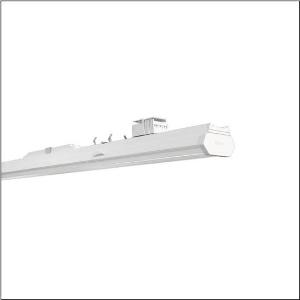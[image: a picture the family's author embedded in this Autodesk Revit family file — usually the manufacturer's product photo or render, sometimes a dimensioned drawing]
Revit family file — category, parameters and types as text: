
# Revit family: licross_r__11_protected_mo_51td117n485g_c933
name_source: partatom
category: Lighting Fixtures
units: mm (PartAtom-declared; Revit-internal decimal feet)

## family parameters
Cut with Voids When Loaded = No
Host = Face
Light Source = No
Part Type = Normal
Room Calculation Point = No
Round Connector Dimension = Use Diameter
Shared = No

## types (1)
- Licross® 11 Protected MO (1 x LED, 8680 lm, 48.6 W, 4000K)
    Apparent Load = 49 VA
    CIE Flux Codes = 83 94 98 100 100
    Color Rendering = 80
    Color Temperature = 4000K
    Default Elevation = 1800 mm
    Description = Licross® 11 Protected MO, luminaire insert, of sheet steel, galvanised, coil coated, white, length: 1.500mm, width: 90mm, height: 101mm, LED rated luminous flux: 8.680lm, light colour: 840, control gear: ON/OFF, with plug, 3-pole, with phase selection, mains connection: 220..240V, AC, 50/60Hz, rated input power: 49W, halogen-free wiring, primary light control with lens, of plastic, primary optical cover: cover, of PMMA, light emission: direct distribution, primary light characteristic: symmetric, protection rating (complete): IP54, insulation class (complete): insulation class I (protective earthing), certification: CE, ENEC, VDE, UKCA, protection symbol: D if used in an environment with non-conductive dust loads with corresponding accessories, impact resistance: IK06, permissible ambient temperature for indoor applications: -25..+35°C, corresponds to IFS (International Featured Standards) requirements for safety and quality in the food industry, reducing of maximum allowable ambient temperature of 5°C with ceiling mounting, LABS conformity tested according to VDMA 24364:2018-05, packaging unit: 1 piece
    Height = 92 mm
    Lamp = 1 x LED
    Lamp Light Flux = 8680 lm
    Lamp Power = 48.6 W
    Lamp count = 1
    Length = 1500 mm
    Luminous efficacy = 179 lm/W
    Manufacturer = Siteco
    ModVariant = No
    Model = 51TD117N485G
    Mounting Place = Ceiling
    Mounting Type = Pendant
    Number of Poles = 1
    OnlyDefault = Yes
    Power Factor = 1
    Product Name = Licross® 11 Protected MO
    Product group = luminaire insert
    ProductGroupID = 901
    Protection Class = Protection class I
    Protection Degree = IP 54
    RLX_Detail_Level = 1
    RLX_Emergency_Light_Flux = 0 lm
    RLX_Emergency_Type = 0
    RLX_Emergency_Type_DB = No
    RlxData = <blob elided: 20385 chars, md5=63f5eba3>
    Socket = socket
    Standby Power = 0 W
    System Light Flux = 8680 lm
    System Power = 49 W
    Type Comments = Product without accessories
    Type Image = l_1256145.jpg
    URL = http://relux.com
    VarID = ---
    Voltage = 0 V
    Weight = 0.00 kg
    Width = 88 mm

## geometry (parser evidence)
native form markers: Blend x4, Sweep x10
no freeform markers — native parametric forms only
